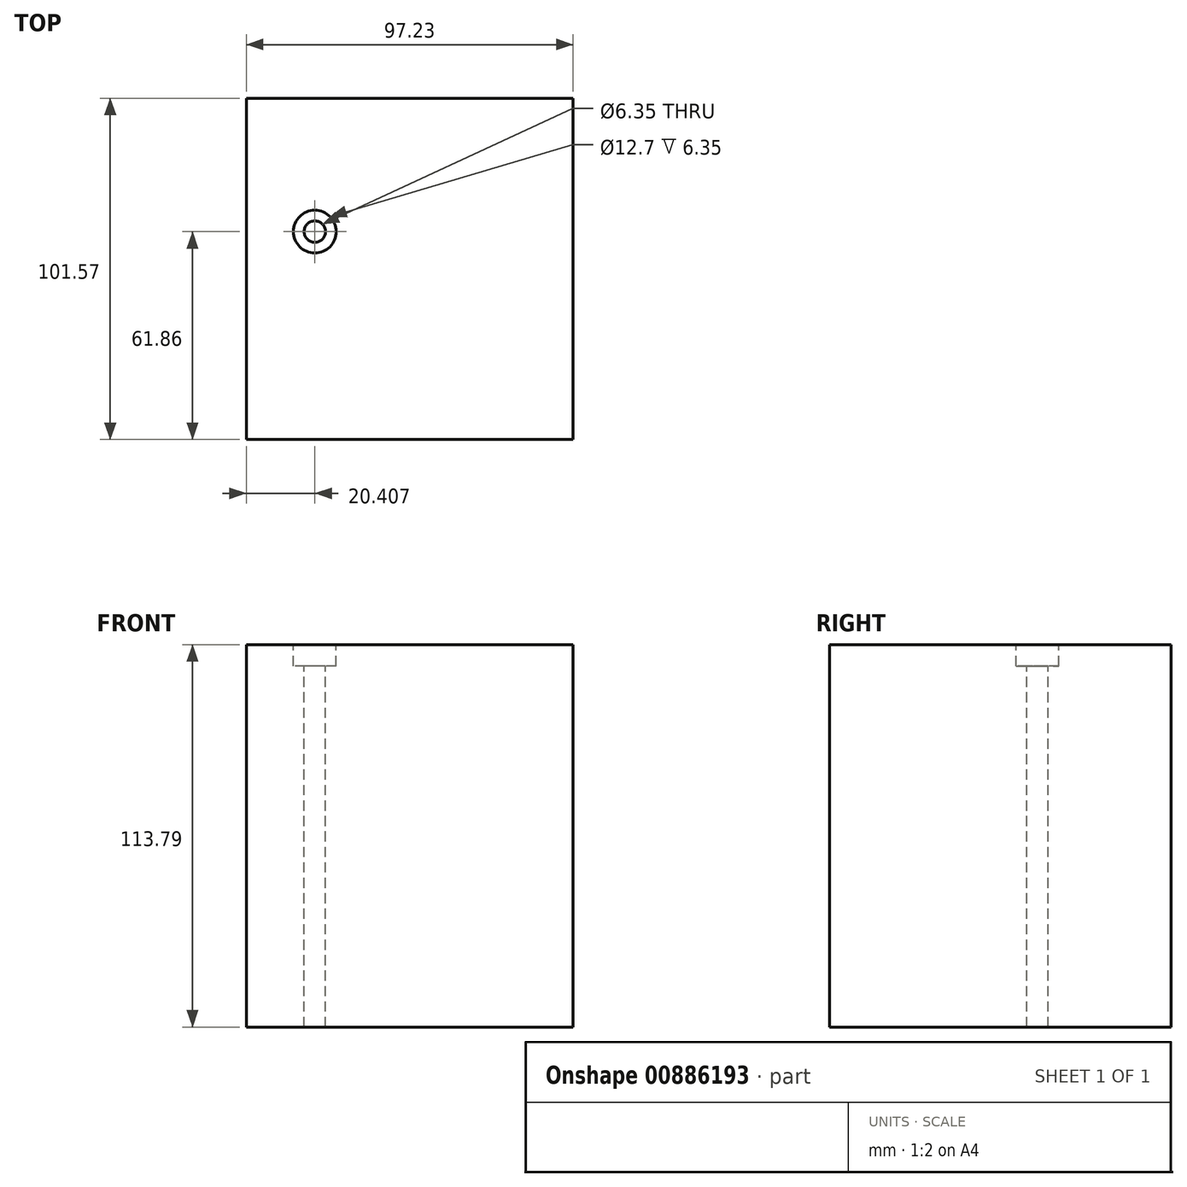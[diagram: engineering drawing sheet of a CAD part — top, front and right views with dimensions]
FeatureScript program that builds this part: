
annotation { "Feature Type Name" : "Feature", "Feature Type Description" : "" }
export const myFeature = defineFeature(function(context is Context, id is Id, definition is map)
    precondition{}
    {
        {
            var Q0;
            Q0=qCreatedBy(makeId("Top.planeOp"),FACE);
            var sketch = newSketch(context, id + "F0", { "sketchPlane" : qUnion([Q0])});
            skLineSegment(sketch, "E0.bottom", {"start": v(-48.04, 52.63) * mm, "end": v(49.19, 52.63) * mm});
            skLineSegment(sketch, "E0.top", {"start": v(-48.04, -48.94) * mm, "end": v(49.19, -48.94) * mm});
            skLineSegment(sketch, "E0.left", {"start": v(-48.04, 52.63) * mm, "end": v(-48.04, -48.94) * mm});
            skLineSegment(sketch, "E0.right", {"start": v(49.19, 52.63) * mm, "end": v(49.19, -48.94) * mm});
            skSolve(sketch);
        }
        {
            var Q0;
            Q0 = qSketchRegion(id + "F0", true);
            extrude(context, id + "F1", {"entities" : qUnion([Q0]), "depth" : 113.8 * mm, "offsetDistance" : 25.4 * mm});
        }
        {
            var Q0;
            Q0=makeQuery(id+"F1.opExtrude","CAP_FACE",FACE,{"disambiguationData":[OSD([sQuery(id+"F0.wireOp",EDGE,"E0.bottom"),sQuery(id+"F0.wireOp",EDGE,"E0.top"),sQuery(id+"F0.wireOp",EDGE,"E0.left"),sQuery(id+"F0.wireOp",EDGE,"E0.right")])],"isStart":false});
            var sketch = newSketch(context, id + "F2", { "sketchPlane" : qUnion([Q0])});
            skPoint(sketch, "E1", {"position": v(-27.63, 12.92) * mm});
            skSolve(sketch);
        }
        {
            var Q0;
            Q0=sQuery(id+"F2.wireOp",VERTEX,"E1");
            var Q1;
            Q1=makeQuery(id+"F1.opExtrude","SWEPT_BODY",BODY,{"disambiguationData":[OSD([sQuery(id+"F0.wireOp",EDGE,"E0.bottom"),sQuery(id+"F0.wireOp",EDGE,"E0.top"),sQuery(id+"F0.wireOp",EDGE,"E0.left"),sQuery(id+"F0.wireOp",EDGE,"E0.right")])]});
            hole(context, id + "F3", {"style" : HoleStyle.C_BORE, "endStyle" : HoleEndStyle.THROUGH, "holeDiameter" : 6.35 * mm, "cBoreDiameter" : 12.7 * mm, "cBoreDepth" : 6.35 * mm, "majorDiameter" : 6.35 * mm, "isTappedThrough" : true, "tappedDepth" : 12.7 * mm, "tapClearance" : 3, "locations" : qUnion([Q0]), "scope" : qUnion([Q1])});
        }
    });
